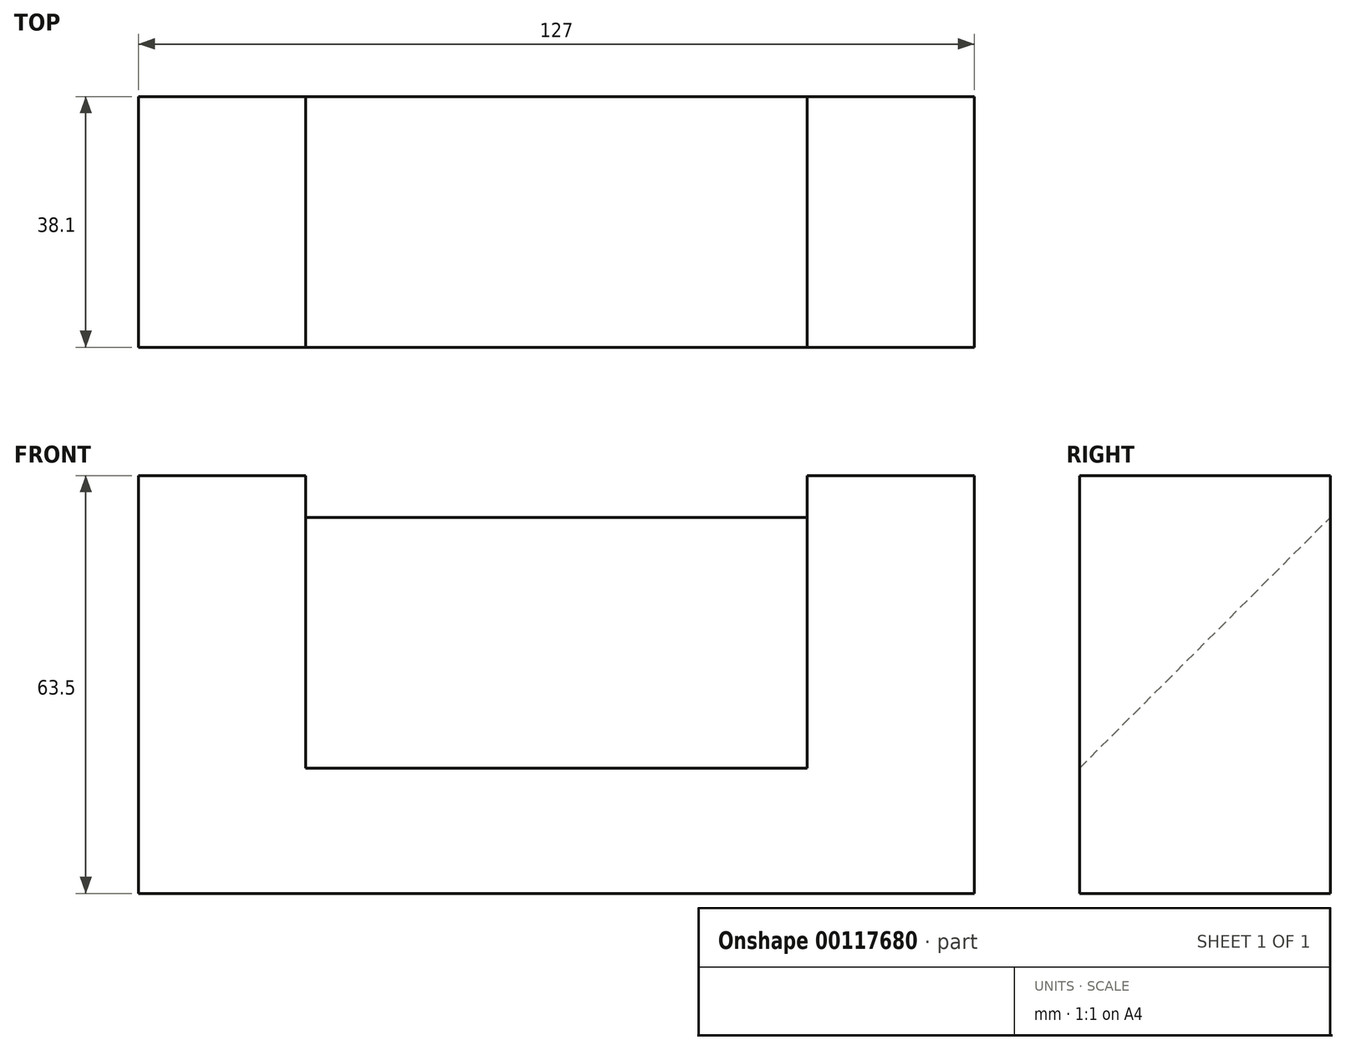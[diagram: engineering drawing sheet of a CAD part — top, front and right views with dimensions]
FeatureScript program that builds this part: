
annotation { "Feature Type Name" : "Feature", "Feature Type Description" : "" }
export const myFeature = defineFeature(function(context is Context, id is Id, definition is map)
    precondition{}
    {
        {
            var Q0;
            Q0=qCreatedBy(makeId("Front.planeOp"),FACE);
            var sketch = newSketch(context, id + "F0", { "sketchPlane" : qUnion([Q0])});
            skLineSegment(sketch, "E0.bottom", {"start": v(63.5, 31.75) * mm, "end": v(-63.5, 31.75) * mm});
            skLineSegment(sketch, "E0.top", {"start": v(63.5, -31.75) * mm, "end": v(-63.5, -31.75) * mm});
            skLineSegment(sketch, "E0.left", {"start": v(63.5, 31.75) * mm, "end": v(63.5, -31.75) * mm});
            skLineSegment(sketch, "E0.right", {"start": v(-63.5, 31.75) * mm, "end": v(-63.5, -31.75) * mm});
            skPoint(sketch, "E0.middle", {"position": v(0, 0) * mm});
            skSolve(sketch);
        }
        {
            var Q0;
            Q0=makeQuery(id+"F0.imprint","IMPRINT",FACE,{"disambiguationData":[TD([[makeQuery(id+"F0.imprint","IMPRINT",EDGE,{"derivedFrom":sQuery(id+"F0.wireOp",EDGE,"E0.bottom")}),1.0]])]});
            extrude(context, id + "F1", {"entities" : qUnion([Q0]), "depth" : 38.1 * mm});
        }
        {
            var Q0;
            Q0=makeQuery(id+"F1.opExtrude","CAP_FACE",FACE,{"disambiguationData":[OSD([sQuery(id+"F0.wireOp",EDGE,"E0.bottom"),sQuery(id+"F0.wireOp",EDGE,"E0.top"),sQuery(id+"F0.wireOp",EDGE,"E0.left"),sQuery(id+"F0.wireOp",EDGE,"E0.right")])],"isStart":false});
            var sketch = newSketch(context, id + "F2", { "sketchPlane" : qUnion([Q0])});
            skLineSegment(sketch, "E1", {"start": v(-63.5, 31.75) * mm, "end": v(-38.1, 31.75) * mm});
            skLineSegment(sketch, "E2", {"start": v(-38.1, 31.75) * mm, "end": v(-38.1, -12.7) * mm});
            skLineSegment(sketch, "E3", {"start": v(-38.1, -12.7) * mm, "end": v(38.1, -12.7) * mm});
            skLineSegment(sketch, "E4", {"start": v(38.1, -12.7) * mm, "end": v(38.1, 31.75) * mm});
            skSolve(sketch);
        }
        {
            var Q0;
            Q0=makeQuery(id+"F1.opExtrude","SWEPT_FACE",FACE,{"disambiguationData":[OSD([sQuery(id+"F0.wireOp",EDGE,"E0.left")])]});
            var sketch = newSketch(context, id + "F3", { "sketchPlane" : qUnion([Q0])});
            skLineSegment(sketch, "E5.bottom", {"start": v(-38.1, 31.75) * mm, "end": v(0, 31.75) * mm});
            skLineSegment(sketch, "E5.top", {"start": v(-38.1, -31.75) * mm, "end": v(0, -31.75) * mm});
            skLineSegment(sketch, "E5.left", {"start": v(-38.1, 31.75) * mm, "end": v(-38.1, -31.75) * mm});
            skLineSegment(sketch, "E5.right", {"start": v(0, 31.75) * mm, "end": v(0, -31.75) * mm});
            skSolve(sketch);
        }
        {
            var Q0;
            Q0 = qSketchRegion(id + "F3", true);
            extrude(context, id + "F4", {"entities" : qUnion([Q0]), "operationType" : NewBodyOperationType.REMOVE, "oppositeDirection" : true, "depth" : 25.4 * mm});
        }
        {
            var Q0;
            Q0=makeQuery(id+"F4.boolean.opBoolean","COPY",FACE,{"derivedFrom":makeQuery(id+"F4.opExtrude","CAP_FACE",FACE,{"disambiguationData":[OSD([sQuery(id+"F3.wireOp",EDGE,"E5.bottom"),sQuery(id+"F3.wireOp",EDGE,"E5.top"),sQuery(id+"F3.wireOp",EDGE,"E5.left"),sQuery(id+"F3.wireOp",EDGE,"E5.right")])],"isStart":false})});
            var sketch = newSketch(context, id + "F5", { "sketchPlane" : qUnion([Q0])});
            skLineSegment(sketch, "E6", {"start": v(-38.1, -31.75) * mm, "end": v(-38.1, -12.7) * mm});
            skLineSegment(sketch, "E7", {"start": v(-38.1, -12.7) * mm, "end": v(0, 25.4) * mm});
            skSolve(sketch);
        }
        {
            var Q0;
            {var subQ0=sQuery(id+"F5.wireOp",EDGE,"E7");Q0=makeQuery(id+"F5.imprint","IMPRINT",FACE,{"disambiguationData":[TD([[makeQuery(id+"F5.imprint","IMPRINT",EDGE,{"derivedFrom":subQ0}),1.0]])]});}
            extrude(context, id + "F6", {"entities" : qUnion([Q0]), "operationType" : NewBodyOperationType.REMOVE, "oppositeDirection" : true, "depth" : 76.2 * mm});
        }
        {
            var Q0;
            Q0=makeQuery(id+"F4.boolean.opBoolean","COPY",FACE,{"derivedFrom":makeQuery(id+"F4.opExtrude","CAP_FACE",FACE,{"disambiguationData":[OSD([sQuery(id+"F3.wireOp",EDGE,"E5.bottom"),sQuery(id+"F3.wireOp",EDGE,"E5.top"),sQuery(id+"F3.wireOp",EDGE,"E5.left"),sQuery(id+"F3.wireOp",EDGE,"E5.right")])],"isStart":false})});
            var sketch = newSketch(context, id + "F7", { "sketchPlane" : qUnion([Q0])});
            skLineSegment(sketch, "E8.bottom", {"start": v(0, -31.75) * mm, "end": v(-38.1, -31.75) * mm});
            skLineSegment(sketch, "E8.top", {"start": v(0, 31.75) * mm, "end": v(-38.1, 31.75) * mm});
            skLineSegment(sketch, "E8.left", {"start": v(0, -31.75) * mm, "end": v(0, 31.75) * mm});
            skLineSegment(sketch, "E8.right", {"start": v(-38.1, -31.75) * mm, "end": v(-38.1, 31.75) * mm});
            skSolve(sketch);
        }
        {
            var Q0;
            {var subQ0=sQuery(id+"F7.wireOp",EDGE,"E8.top");Q0=makeQuery(id+"F7.imprint","IMPRINT",FACE,{"disambiguationData":[TD([[makeQuery(id+"F7.imprint","IMPRINT",EDGE,{"derivedFrom":subQ0}),1.0]])]});}
            var Q1;
            {var subQ0=sQuery(id+"F7.wireOp",EDGE,"E8.bottom");Q1=makeQuery(id+"F7.imprint","IMPRINT",FACE,{"disambiguationData":[TD([[makeQuery(id+"F7.imprint","IMPRINT",EDGE,{"derivedFrom":subQ0}),1.0]])]});}
            extrude(context, id + "F8", {"entities" : qUnion([Q0, Q1]), "operationType" : NewBodyOperationType.ADD, "depth" : 25.4 * mm});
        }
    });
